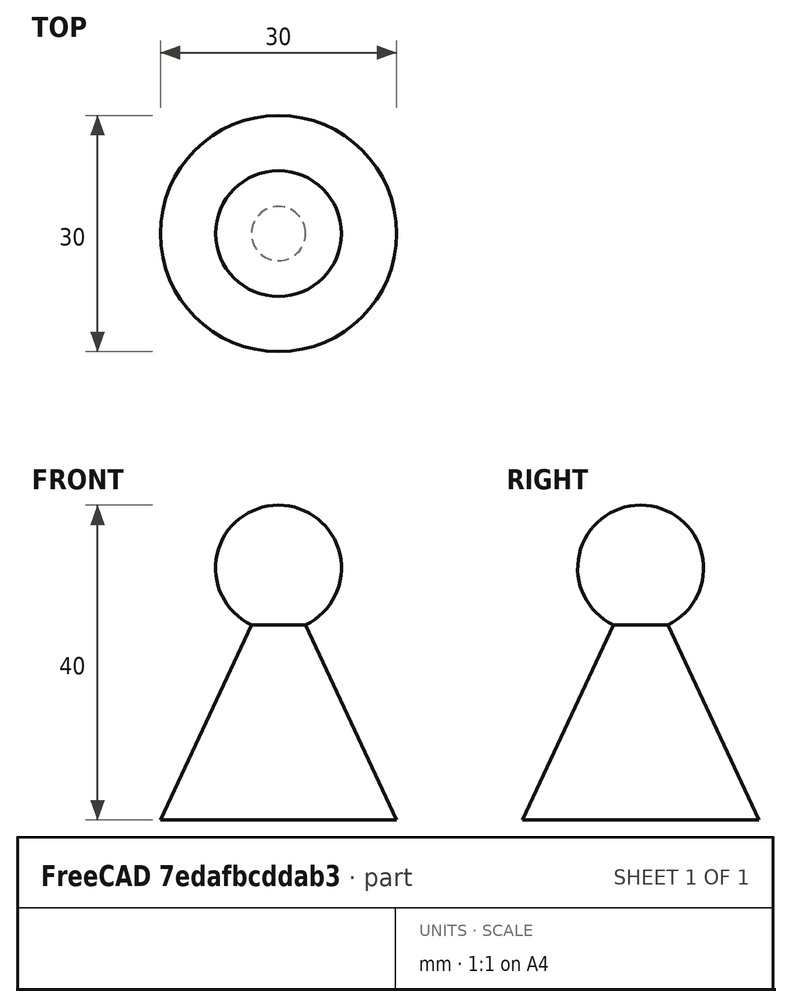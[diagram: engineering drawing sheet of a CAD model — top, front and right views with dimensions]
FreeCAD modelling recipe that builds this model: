
FCSTD DOCUMENT  (FreeCAD 1.0R38806 (Git))
Label: reto_5
License: All rights reserved
LicenseURL: https://en.wikipedia.org/wiki/All_rights_reserved
objects: Sketcher::SketchObject×1, Part::Revolution×1
note: 3 computed .brp shape members not serialized (recipe doc carries the construction recipe); baked Part::Feature solids carry a one-line shape summary decoded from their .brp

FEATURE [Sketcher::SketchObject] Sketch
  ArcFitTolerance = 1e-06
  FullyConstrained = false
  MakeInternals = false
  Placement = pos=(0,0,0) rot=(1,0,0;1.5708rad)
  sketch-geometry (4):
    g0: LineSegment StartX=2.4e-15 StartY=0 StartZ=0 EndX=2.4e-15 EndY=40 EndZ=0
    g1: LineSegment StartX=2.4e-15 StartY=0 StartZ=0 EndX=15 EndY=0 EndZ=0
    g2: ArcOfCircle CenterX=0 CenterY=32 CenterZ=0 NormalX=0 NormalY=0 NormalZ=1 AngleXU=0 Radius=8 StartAngle=5.15757 EndAngle=7.85398
    g3: LineSegment StartX=3.445 StartY=24.7798 StartZ=0 EndX=15 EndY=0 EndZ=0
  constraints (11):
    c: Distance(g0) = 40
    c: Coincident(g0,g-1)
    c: Vertical(g0)
    c: Distance(g1) = 15
    c: Coincident(g1,g0)
    c: PointOnObject(g1,g-1)
    c: Radius(g2) = 8
    c: PointOnObject(g2,g0)
    c: Coincident(g2,g0)
    c: Coincident(g3,g2)
    c: Coincident(g3,g1)
FEATURE [Part::Revolution] Revolve
  Angle = 360
  Axis = (0,0,1)
  Base = (0,0,0)
  FaceMakerClass = Part::FaceMakerBullseye
  Solid = true
  Source = -> Sketch
  Symmetric = false
